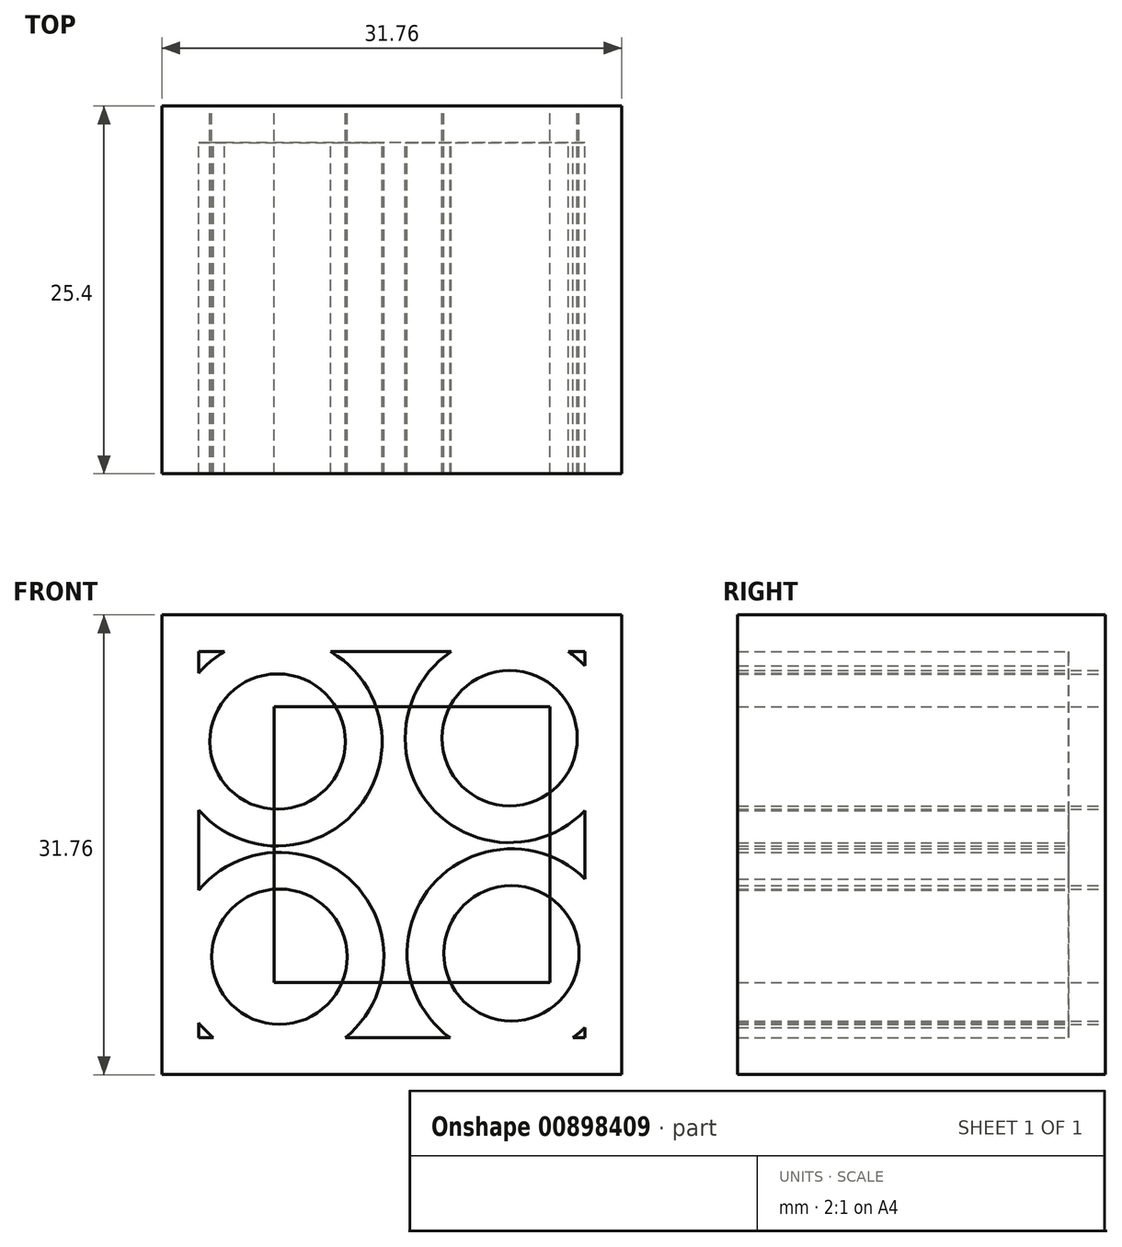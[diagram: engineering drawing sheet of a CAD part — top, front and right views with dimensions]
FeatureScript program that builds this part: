
annotation { "Feature Type Name" : "Feature", "Feature Type Description" : "" }
export const myFeature = defineFeature(function(context is Context, id is Id, definition is map)
    precondition{}
    {
        {
            var Q0;
            Q0=qCreatedBy(makeId("Front.planeOp"),FACE);
            var sketch = newSketch(context, id + "F0", { "sketchPlane" : qUnion([Q0])});
            skLineSegment(sketch, "E0.bottom", {"start": v(10.91, 9.52) * mm, "end": v(-8.14, 9.52) * mm});
            skLineSegment(sketch, "E0.top", {"start": v(10.91, -9.53) * mm, "end": v(-8.14, -9.53) * mm});
            skLineSegment(sketch, "E0.left", {"start": v(10.91, 9.53) * mm, "end": v(10.91, -9.52) * mm});
            skLineSegment(sketch, "E0.right", {"start": v(-8.14, 9.52) * mm, "end": v(-8.14, -9.53) * mm});
            skPoint(sketch, "E0.middle", {"position": v(1.39, 0) * mm});
            skSolve(sketch);
        }
        {
            var Q0;
            Q0=qCreatedBy(makeId("Front.planeOp"),FACE);
            var sketch = newSketch(context, id + "F1", { "sketchPlane" : qUnion([Q0])});
            skLineSegment(sketch, "E1.bottom", {"start": v(15.87, 15.88) * mm, "end": v(-15.88, 15.88) * mm});
            skLineSegment(sketch, "E1.top", {"start": v(15.88, -15.88) * mm, "end": v(-15.87, -15.88) * mm});
            skLineSegment(sketch, "E1.left", {"start": v(15.87, 15.88) * mm, "end": v(15.88, -15.88) * mm});
            skLineSegment(sketch, "E1.right", {"start": v(-15.88, 15.88) * mm, "end": v(-15.87, -15.88) * mm});
            skPoint(sketch, "E1.middle", {"position": v(0, 0) * mm});
            skCircle(sketch, "E2", {"center": v(-7.9, 7.13) * mm, "radius": 4.67 * mm});
            skCircle(sketch, "E3", {"center": v(-7.9, 7.13) * mm, "radius": 3.56 * mm});
            skCircle(sketch, "E4.1.0.0", {"center": v(8.13, 7.37) * mm, "radius": 4.67 * mm});
            skCircle(sketch, "E4.1.0.1", {"center": v(8.13, 7.37) * mm, "radius": 3.56 * mm});
            skLineSegment(sketch, "E4.direction1", {"start": v(-7.9, 7.13) * mm, "end": v(8.13, 7.37) * mm, "construction": true});
            skLineSegment(sketch, "E5.0.1.0", {"start": v(16, 1.02) * mm, "end": v(-15.75, 1.02) * mm});
            skLineSegment(sketch, "E5.0.1.1", {"start": v(16, 1.02) * mm, "end": v(16, -30.73) * mm});
            skLineSegment(sketch, "E5.0.1.2", {"start": v(-7.77, -7.73) * mm, "end": v(8.25, -7.5) * mm, "construction": true});
            skLineSegment(sketch, "E5.0.1.3", {"start": v(-15.75, 1.02) * mm, "end": v(-15.75, -30.73) * mm});
            skCircle(sketch, "E5.0.1.4", {"center": v(-7.77, -7.73) * mm, "radius": 3.56 * mm});
            skCircle(sketch, "E5.0.1.5", {"center": v(-7.77, -7.73) * mm, "radius": 4.67 * mm});
            skPoint(sketch, "E5.0.1.6", {"position": v(0.13, -14.86) * mm});
            skCircle(sketch, "E5.0.1.7", {"center": v(8.25, -7.5) * mm, "radius": 3.56 * mm});
            skCircle(sketch, "E5.0.1.8", {"center": v(8.25, -7.5) * mm, "radius": 4.67 * mm});
            skLineSegment(sketch, "E5.direction1", {"start": v(-15.88, -15.88) * mm, "end": v(45.92, -18.24) * mm, "construction": true});
            skLineSegment(sketch, "E5.direction2", {"start": v(-15.87, -15.88) * mm, "end": v(-15.75, -30.73) * mm, "construction": true});
            skSolve(sketch);
        }
        {
            var Q0;
            Q0 = qSketchRegion(id + "F1", true);
            extrude(context, id + "F2", {"entities" : qUnion([Q0]), "depth" : 25.4 * mm, "offsetDistance" : 25.4 * mm});
        }
        {
            var Q0;
            Q0=makeQuery(id+"F2.opExtrude","CAP_FACE",FACE,{"disambiguationData":[OSD([sQuery(id+"F1.wireOp",EDGE,"E1.bottom"),sQuery(id+"F1.wireOp",EDGE,"E1.top"),sQuery(id+"F1.wireOp",EDGE,"E1.left"),sQuery(id+"F1.wireOp",EDGE,"E1.right"),sQuery(id+"F1.wireOp",EDGE,"E2"),sQuery(id+"F1.wireOp",EDGE,"E4.1.0.0"),sQuery(id+"F1.wireOp",EDGE,"E5.0.1.5"),sQuery(id+"F1.wireOp",EDGE,"E5.0.1.8")])],"isStart":false});
            shell(context, id + "F3", {"entities" : qUnion([Q0]), "thickness" : 2.54 * mm});
        }
        {
            var Q0;
            Q0=sQuery(id+"F1.wireOp",EDGE,"E3");
            var Q1;
            Q1=sQuery(id+"F1.wireOp",EDGE,"E2");
            extrude(context, id + "F4", {"bodyType" : ToolBodyType.SURFACE, "surfaceEntities" : qUnion([Q0, Q1]), "depth" : 25.4 * mm, "offsetDistance" : 25.4 * mm});
        }
        {
            var Q0;
            Q0 = qSketchRegion(id + "F0", true);
            extrude(context, id + "F5", {"entities" : qUnion([Q0]), "depth" : 25.4 * mm, "offsetDistance" : 25.4 * mm});
        }
    });
